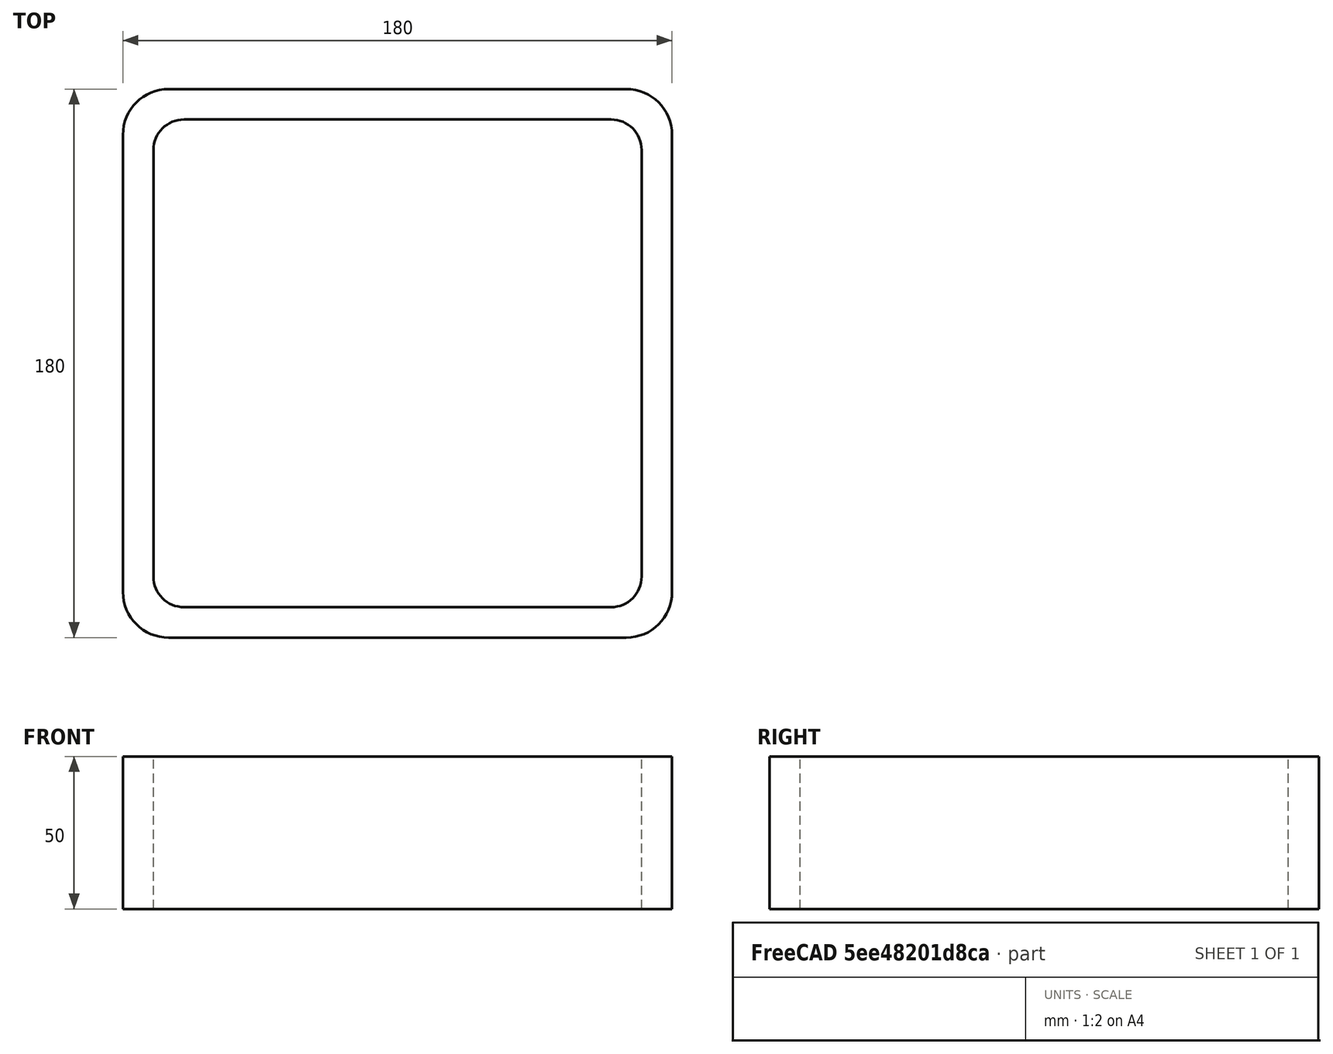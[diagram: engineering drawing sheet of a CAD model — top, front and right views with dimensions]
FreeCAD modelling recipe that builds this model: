
FCSTD DOCUMENT  (FreeCAD 0.15R4671 (Git))
Label: Square hollow section 180x180x10 EN10219 S235JRH
License: All rights reserved
LicenseURL: http://en.wikipedia.org/wiki/All_rights_reserved
objects: Sketcher::SketchObject×1, Part::Extrusion×1
note: 2 computed .brp shape members not serialized (recipe doc carries the construction recipe); baked Part::Feature solids carry a one-line shape summary decoded from their .brp

FEATURE [Sketcher::SketchObject] Sketch
  sketch-geometry (16):
    g0: LineSegment StartX=-70 StartY=80 StartZ=0 EndX=70 EndY=80 EndZ=0
    g1: LineSegment StartX=80 StartY=70 StartZ=0 EndX=80 EndY=-70 EndZ=0
    g2: LineSegment StartX=70 StartY=-80 StartZ=0 EndX=-70 EndY=-80 EndZ=0
    g3: LineSegment StartX=-80 StartY=-70 StartZ=0 EndX=-80 EndY=70 EndZ=0
    g4: LineSegment StartX=-75 StartY=90 StartZ=0 EndX=75 EndY=90 EndZ=0
    g5: LineSegment StartX=90 StartY=75 StartZ=0 EndX=90 EndY=-75 EndZ=0
    g6: LineSegment StartX=75 StartY=-90 StartZ=0 EndX=-75 EndY=-90 EndZ=0
    g7: LineSegment StartX=-90 StartY=-75 StartZ=0 EndX=-90 EndY=75 EndZ=0
    g8: ArcOfCircle CenterX=-70 CenterY=70 CenterZ=0 NormalX=0 NormalY=0 NormalZ=1 Radius=10 StartAngle=1.5708 EndAngle=3.14159
    g9: ArcOfCircle CenterX=70 CenterY=70 CenterZ=0 NormalX=0 NormalY=0 NormalZ=1 Radius=10 StartAngle=0 EndAngle=1.5708
    g10: ArcOfCircle CenterX=70 CenterY=-70 CenterZ=0 NormalX=0 NormalY=0 NormalZ=1 Radius=10 StartAngle=4.71239 EndAngle=6.28319
    g11: ArcOfCircle CenterX=-70 CenterY=-70 CenterZ=0 NormalX=0 NormalY=0 NormalZ=1 Radius=10 StartAngle=3.14159 EndAngle=4.71239
    g12: ArcOfCircle CenterX=75 CenterY=75 CenterZ=0 NormalX=0 NormalY=0 NormalZ=1 Radius=15 StartAngle=0 EndAngle=1.5708
    g13: ArcOfCircle CenterX=75 CenterY=-75 CenterZ=0 NormalX=0 NormalY=0 NormalZ=1 Radius=15 StartAngle=4.71239 EndAngle=6.28319
    g14: ArcOfCircle CenterX=-75 CenterY=-75 CenterZ=0 NormalX=0 NormalY=0 NormalZ=1 Radius=15 StartAngle=3.14159 EndAngle=4.71239
    g15: ArcOfCircle CenterX=-75 CenterY=75 CenterZ=0 NormalX=0 NormalY=0 NormalZ=1 Radius=15 StartAngle=1.5708 EndAngle=3.14159
  constraints (36):
    c: Horizontal(g2)
    c: Vertical(g3)
    c: Horizontal(g6)
    c: Vertical(g7)
    c: Tangent(g3,g8) = 1.5708
    c: Tangent(g0,g8) = 1.5708
    c: Tangent(g0,g9) = 1.5708
    c: Tangent(g1,g9) = 1.5708
    c: Tangent(g1,g10) = 1.5708
    c: Tangent(g2,g10) = 1.5708
    c: Tangent(g2,g11) = 1.5708
    c: Tangent(g3,g11) = 1.5708
    c: Tangent(g4,g12) = 1.5708
    c: Tangent(g5,g12) = 1.5708
    c: Tangent(g5,g13) = 1.5708
    c: Tangent(g6,g13) = 1.5708
    c: Tangent(g6,g14) = 1.5708
    c: Tangent(g7,g14) = 1.5708
    c: Tangent(g7,g15) = 1.5708
    c: Tangent(g4,g15) = 1.5708
    c: Equal(g9,g8)
    c: Equal(g9,g11)
    c: Equal(g9,g10)
    c: Equal(g12,g15)
    c: Equal(g12,g14)
    c: Equal(g12,g13)
    c: Symmetric(g4,g6,g-1)
    c: Symmetric(g7,g5,g-2)
    c: DistanceY(g4,g6) = -180
    c: DistanceX(g7,g5) = 180
    c: Symmetric(g3,g1,g-2)
    c: Symmetric(g0,g2,g-1)
    c: DistanceY(g0,g4) = 10
    c: DistanceX(g5,g1) = -10
    c: Radius(g9) = 10
    c: Radius(g12) = 15
FEATURE [Part::Extrusion] Extrude  label="Square hollow section 180x180x10 EN10219 S235JRH"
  Base = -> Sketch
  Dir = (0,0,50)
  Solid = true
